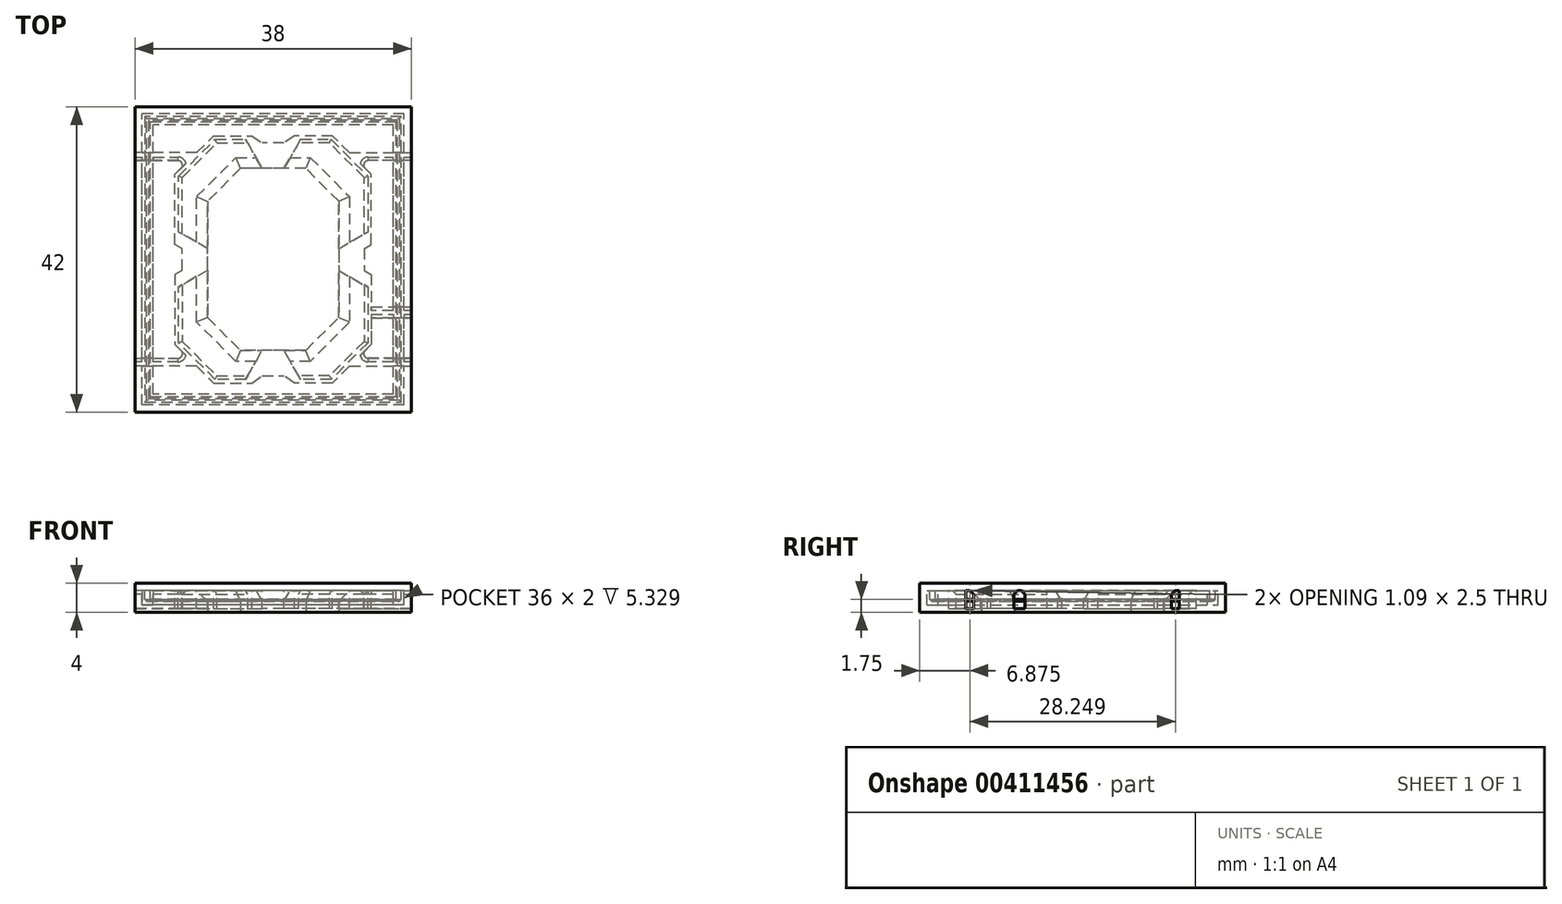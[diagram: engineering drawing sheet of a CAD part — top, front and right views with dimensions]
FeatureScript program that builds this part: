
annotation { "Feature Type Name" : "Feature", "Feature Type Description" : "" }
export const myFeature = defineFeature(function(context is Context, id is Id, definition is map)
    precondition{}
    {
        {
            var Q0;
            Q0=qCreatedBy(makeId("Top.planeOp"),FACE);
            var sketch = newSketch(context, id + "F0", { "sketchPlane" : qUnion([Q0])});
            skLineSegment(sketch, "E0.bottom", {"start": v(19, -21) * mm, "end": v(-19, -21) * mm});
            skLineSegment(sketch, "E0.top", {"start": v(19, 21) * mm, "end": v(-19, 21) * mm});
            skLineSegment(sketch, "E0.left", {"start": v(19, -21) * mm, "end": v(19, 21) * mm});
            skLineSegment(sketch, "E0.right", {"start": v(-19, -21) * mm, "end": v(-19, 21) * mm});
            skPoint(sketch, "E0.middle", {"position": v(0, 0) * mm});
            skLineSegment(sketch, "E1", {"start": v(4.5, 12.5) * mm, "end": v(9, 8) * mm});
            skLineSegment(sketch, "E2", {"start": v(4.5, 12.5) * mm, "end": v(0, 12.5) * mm});
            skLineSegment(sketch, "E3", {"start": v(9, 8) * mm, "end": v(9, 0) * mm});
            skLineSegment(sketch, "E4.MirrorCS", {"start": v(-9, 8) * mm, "end": v(-9, 0) * mm});
            skLineSegment(sketch, "E5.MirrorCS", {"start": v(-4.5, 12.5) * mm, "end": v(-9, 8) * mm});
            skLineSegment(sketch, "E6.MirrorCS", {"start": v(-4.5, 12.5) * mm, "end": v(0, 12.5) * mm});
            skLineSegment(sketch, "E7.MirrorCS", {"start": v(-9, -8) * mm, "end": v(-9, 0) * mm});
            skLineSegment(sketch, "E8.MirrorCS", {"start": v(4.5, -12.5) * mm, "end": v(9, -8) * mm});
            skLineSegment(sketch, "E9.MirrorCS", {"start": v(9, -8) * mm, "end": v(9, 0) * mm});
            skLineSegment(sketch, "E10.MirrorCS", {"start": v(-4.5, -12.5) * mm, "end": v(-9, -8) * mm});
            skLineSegment(sketch, "E11.MirrorCS", {"start": v(-4.5, -12.5) * mm, "end": v(0, -12.5) * mm});
            skLineSegment(sketch, "E12.MirrorCS", {"start": v(4.5, -12.5) * mm, "end": v(0, -12.5) * mm});
            skSolve(sketch);
        }
        {
            var Q0;
            Q0 = qSketchRegion(id + "F0", true);
            extrude(context, id + "F1", {"entities" : qUnion([Q0]), "depth" : 3 * mm, "offsetDistance" : 25 * mm});
        }
        {
            var Q0;
            Q0=makeQuery(id+"F1.opExtrude","CAP_FACE",FACE,{"disambiguationData":[OSD([sQuery(id+"F0.wireOp",EDGE,"E0.bottom"),sQuery(id+"F0.wireOp",EDGE,"E0.top"),sQuery(id+"F0.wireOp",EDGE,"E0.left"),sQuery(id+"F0.wireOp",EDGE,"E0.right"),sQuery(id+"F0.wireOp",EDGE,"E1"),sQuery(id+"F0.wireOp",EDGE,"E2"),sQuery(id+"F0.wireOp",EDGE,"E3"),sQuery(id+"F0.wireOp",EDGE,"E4.MirrorCS"),sQuery(id+"F0.wireOp",EDGE,"E5.MirrorCS"),sQuery(id+"F0.wireOp",EDGE,"E6.MirrorCS"),sQuery(id+"F0.wireOp",EDGE,"E7.MirrorCS"),sQuery(id+"F0.wireOp",EDGE,"E8.MirrorCS"),sQuery(id+"F0.wireOp",EDGE,"E9.MirrorCS"),sQuery(id+"F0.wireOp",EDGE,"E10.MirrorCS"),sQuery(id+"F0.wireOp",EDGE,"E11.MirrorCS"),sQuery(id+"F0.wireOp",EDGE,"E12.MirrorCS")])],"isStart":false});
            var sketch = newSketch(context, id + "F2", { "sketchPlane" : qUnion([Q0])});
            skLineSegment(sketch, "E13", {"start": v(9, 1.5) * mm, "end": v(12.5, 3.5) * mm});
            skLineSegment(sketch, "E14", {"start": v(12.5, 3.5) * mm, "end": v(12.5, 11.26) * mm});
            skLineSegment(sketch, "E15", {"start": v(7.76, 16) * mm, "end": v(3.5, 16) * mm});
            skLineSegment(sketch, "E16", {"start": v(3.5, 16) * mm, "end": v(1.5, 12.5) * mm});
            skLineSegment(sketch, "E17", {"start": v(12.5, 1.5) * mm, "end": v(13.5, 2.07) * mm});
            skLineSegment(sketch, "E18", {"start": v(13.5, 2.07) * mm, "end": v(13.5, 11.67) * mm});
            skLineSegment(sketch, "E19", {"start": v(8.17, 17) * mm, "end": v(2.91, 17) * mm});
            skLineSegment(sketch, "E20", {"start": v(2.91, 17) * mm, "end": v(1.5, 16) * mm});
            skLineSegment(sketch, "E21", {"start": v(1.5, 16) * mm, "end": v(0, 16) * mm});
            skLineSegment(sketch, "E22", {"start": v(1.5, 12.5) * mm, "end": v(0, 12.5) * mm});
            skLineSegment(sketch, "E23", {"start": v(9, 0) * mm, "end": v(9, 1.5) * mm});
            skLineSegment(sketch, "E24", {"start": v(12.5, 0) * mm, "end": v(12.5, 1.5) * mm});
            skLineSegment(sketch, "E25", {"start": v(12.5, 11.26) * mm, "end": v(7.76, 16) * mm});
            skLineSegment(sketch, "E26", {"start": v(13.5, 11.67) * mm, "end": v(12.54, 12.64) * mm});
            skLineSegment(sketch, "E27", {"start": v(10.5, 14.67) * mm, "end": v(19, 14.67) * mm});
            skLineSegment(sketch, "E28", {"start": v(19, 14.67) * mm, "end": v(19, 13.58) * mm});
            skLineSegment(sketch, "E29", {"start": v(19, 13.58) * mm, "end": v(13.06, 13.58) * mm});
            skArc(sketch, "E30", {"start": v(13.06, 13.58) * mm, "mid": v(12.53, 13.25) * mm, "end": v(12.54, 12.64) * mm});
            skLineSegment(sketch, "E31.trimOffspring", {"start": v(10.5, 14.67) * mm, "end": v(8.17, 17) * mm});
            skArc(sketch, "E32.MirrorCS", {"start": v(-13.06, 13.58) * mm, "mid": v(-12.53, 13.25) * mm, "end": v(-12.54, 12.64) * mm});
            skLineSegment(sketch, "E33.MirrorCS", {"start": v(-9, 1.5) * mm, "end": v(-12.5, 3.5) * mm});
            skLineSegment(sketch, "E34.MirrorCS", {"start": v(-7.76, 16) * mm, "end": v(-3.5, 16) * mm});
            skLineSegment(sketch, "E35.MirrorCS", {"start": v(-19, 14.67) * mm, "end": v(-19, 13.58) * mm});
            skLineSegment(sketch, "E36.MirrorCS", {"start": v(-12.5, 3.5) * mm, "end": v(-12.5, 11.26) * mm});
            skLineSegment(sketch, "E37.MirrorCS", {"start": v(-19, 13.58) * mm, "end": v(-13.06, 13.58) * mm});
            skLineSegment(sketch, "E38.MirrorCS", {"start": v(-9, 0) * mm, "end": v(-9, 1.5) * mm});
            skLineSegment(sketch, "E39.MirrorCS", {"start": v(-8.17, 17) * mm, "end": v(-2.91, 17) * mm});
            skLineSegment(sketch, "E40.MirrorCS", {"start": v(-10.5, 14.67) * mm, "end": v(-8.17, 17) * mm});
            skLineSegment(sketch, "E41.MirrorCS", {"start": v(-1.5, 16) * mm, "end": v(0, 16) * mm});
            skLineSegment(sketch, "E42.MirrorCS", {"start": v(-12.5, 11.26) * mm, "end": v(-7.76, 16) * mm});
            skLineSegment(sketch, "E43.MirrorCS", {"start": v(-1.5, 12.5) * mm, "end": v(0, 12.5) * mm});
            skLineSegment(sketch, "E44.MirrorCS", {"start": v(-2.91, 17) * mm, "end": v(-1.5, 16) * mm});
            skLineSegment(sketch, "E45.MirrorCS", {"start": v(-10.5, 14.67) * mm, "end": v(-19, 14.67) * mm});
            skLineSegment(sketch, "E46.MirrorCS", {"start": v(-12.5, 1.5) * mm, "end": v(-13.5, 2.07) * mm});
            skLineSegment(sketch, "E47.MirrorCS", {"start": v(-13.5, 2.07) * mm, "end": v(-13.5, 11.67) * mm});
            skLineSegment(sketch, "E48.MirrorCS", {"start": v(-12.5, 0) * mm, "end": v(-12.5, 1.5) * mm});
            skLineSegment(sketch, "E49.MirrorCS", {"start": v(-3.5, 16) * mm, "end": v(-1.5, 12.5) * mm});
            skLineSegment(sketch, "E50.MirrorCS", {"start": v(-13.5, 11.67) * mm, "end": v(-12.54, 12.64) * mm});
            skLineSegment(sketch, "E51.MirrorCS", {"start": v(-12.5, -1.5) * mm, "end": v(-13.5, -2.07) * mm});
            skLineSegment(sketch, "E52.MirrorCS", {"start": v(19, -14.67) * mm, "end": v(19, -13.58) * mm});
            skLineSegment(sketch, "E53.MirrorCS", {"start": v(-19, -14.67) * mm, "end": v(-19, -13.58) * mm});
            skLineSegment(sketch, "E54.MirrorCS", {"start": v(12.5, -1.5) * mm, "end": v(13.5, -2.07) * mm});
            skArc(sketch, "E55.MirrorCS", {"start": v(-13.06, -13.58) * mm, "mid": v(-12.53, -13.25) * mm, "end": v(-12.54, -12.64) * mm});
            skArc(sketch, "E56.MirrorCS", {"start": v(13.06, -13.58) * mm, "mid": v(12.53, -13.25) * mm, "end": v(12.54, -12.64) * mm});
            skLineSegment(sketch, "E57.MirrorCS", {"start": v(-1.5, -12.5) * mm, "end": v(0, -12.5) * mm});
            skLineSegment(sketch, "E58.MirrorCS", {"start": v(-1.5, -16) * mm, "end": v(0, -16) * mm});
            skLineSegment(sketch, "E59.MirrorCS", {"start": v(-12.5, 0) * mm, "end": v(-12.5, -1.5) * mm});
            skLineSegment(sketch, "E60.MirrorCS", {"start": v(-9, 0) * mm, "end": v(-9, -1.5) * mm});
            skLineSegment(sketch, "E61.MirrorCS", {"start": v(12.5, 0) * mm, "end": v(12.5, -1.5) * mm});
            skLineSegment(sketch, "E62.MirrorCS", {"start": v(9, 0) * mm, "end": v(9, -1.5) * mm});
            skLineSegment(sketch, "E63.MirrorCS", {"start": v(-7.76, -16) * mm, "end": v(-3.5, -16) * mm});
            skLineSegment(sketch, "E64.MirrorCS", {"start": v(3.5, -16) * mm, "end": v(1.5, -12.5) * mm});
            skLineSegment(sketch, "E65.MirrorCS", {"start": v(1.5, -12.5) * mm, "end": v(0, -12.5) * mm});
            skLineSegment(sketch, "E66.MirrorCS", {"start": v(10.5, -14.67) * mm, "end": v(8.17, -17) * mm});
            skLineSegment(sketch, "E67.MirrorCS", {"start": v(7.76, -16) * mm, "end": v(3.5, -16) * mm});
            skLineSegment(sketch, "E68.MirrorCS", {"start": v(13.5, -11.67) * mm, "end": v(12.54, -12.64) * mm});
            skLineSegment(sketch, "E69.MirrorCS", {"start": v(12.5, -11.26) * mm, "end": v(7.76, -16) * mm});
            skLineSegment(sketch, "E70.MirrorCS", {"start": v(-2.91, -17) * mm, "end": v(-1.5, -16) * mm});
            skLineSegment(sketch, "E71.MirrorCS", {"start": v(19, -13.58) * mm, "end": v(13.06, -13.58) * mm});
            skLineSegment(sketch, "E72.MirrorCS", {"start": v(-13.5, -2.07) * mm, "end": v(-13.5, -11.67) * mm});
            skLineSegment(sketch, "E73.MirrorCS", {"start": v(-12.5, -3.5) * mm, "end": v(-12.5, -11.26) * mm});
            skLineSegment(sketch, "E74.MirrorCS", {"start": v(2.91, -17) * mm, "end": v(1.5, -16) * mm});
            skLineSegment(sketch, "E75.MirrorCS", {"start": v(13.5, -2.07) * mm, "end": v(13.5, -11.67) * mm});
            skLineSegment(sketch, "E76.MirrorCS", {"start": v(-8.17, -17) * mm, "end": v(-2.91, -17) * mm});
            skLineSegment(sketch, "E77.MirrorCS", {"start": v(-9, -1.5) * mm, "end": v(-12.5, -3.5) * mm});
            skLineSegment(sketch, "E78.MirrorCS", {"start": v(1.5, -16) * mm, "end": v(0, -16) * mm});
            skLineSegment(sketch, "E79.MirrorCS", {"start": v(-3.5, -16) * mm, "end": v(-1.5, -12.5) * mm});
            skLineSegment(sketch, "E80.MirrorCS", {"start": v(-12.5, -11.26) * mm, "end": v(-7.76, -16) * mm});
            skLineSegment(sketch, "E81.MirrorCS", {"start": v(8.17, -17) * mm, "end": v(2.91, -17) * mm});
            skLineSegment(sketch, "E82.MirrorCS", {"start": v(-19, -13.58) * mm, "end": v(-13.06, -13.58) * mm});
            skLineSegment(sketch, "E83.MirrorCS", {"start": v(10.5, -14.67) * mm, "end": v(19, -14.67) * mm});
            skLineSegment(sketch, "E84.MirrorCS", {"start": v(-10.5, -14.67) * mm, "end": v(-8.17, -17) * mm});
            skLineSegment(sketch, "E85.MirrorCS", {"start": v(12.5, -3.5) * mm, "end": v(12.5, -11.26) * mm});
            skLineSegment(sketch, "E86.MirrorCS", {"start": v(9, -1.5) * mm, "end": v(12.5, -3.5) * mm});
            skLineSegment(sketch, "E87.MirrorCS", {"start": v(-13.5, -11.67) * mm, "end": v(-12.54, -12.64) * mm});
            skLineSegment(sketch, "E88.MirrorCS", {"start": v(-10.5, -14.67) * mm, "end": v(-19, -14.67) * mm});
            skLineSegment(sketch, "E89.bottom", {"start": v(13.5, -6.55) * mm, "end": v(19, -6.55) * mm});
            skLineSegment(sketch, "E89.top", {"start": v(13.5, -8.05) * mm, "end": v(19, -8.05) * mm});
            skLineSegment(sketch, "E89.left", {"start": v(13.5, -6.55) * mm, "end": v(13.5, -8.05) * mm});
            skLineSegment(sketch, "E89.right", {"start": v(19, -6.55) * mm, "end": v(19, -8.05) * mm});
            skSolve(sketch);
        }
        {
            var Q0;
            Q0 = qSketchRegion(id + "F2", true);
            extrude(context, id + "F3", {"entities" : qUnion([Q0]), "oppositeDirection" : true, "depth" : 2.5 * mm, "offsetDistance" : 25 * mm});
        }
        {
            var Q0;
            Q0=makeQuery(id+"F1.opExtrude","CAP_EDGE",EDGE,{"disambiguationData":[OSD([sQuery(id+"F0.wireOp",EDGE,"E5.MirrorCS")])],"isStart":false});
            var Q1;
            {var subQ0=sQuery(id+"F0.wireOp",EDGE,"E6.MirrorCS");var subQ1=sQuery(id+"F0.wireOp",EDGE,"E5.MirrorCS");var subQ2=sQuery(id+"F0.wireOp",EDGE,"E2");Q1=makeQuery(id+"F3.boolean.opBoolean","SPLIT",EDGE,{"disambiguationData":[TD([makeQuery(id+"F1.opExtrude","SWEPT_FACE",FACE,{"disambiguationData":[OSD([subQ1])]})])],"derivedFrom":makeQuery(id+"F1.opExtrude","CAP_EDGE",EDGE,{"disambiguationData":[OSD([subQ2,subQ0])],"isStart":false})});}
            var Q2;
            {var subQ0=sQuery(id+"F0.wireOp",EDGE,"E7.MirrorCS");var subQ1=sQuery(id+"F0.wireOp",EDGE,"E5.MirrorCS");var subQ2=sQuery(id+"F0.wireOp",EDGE,"E4.MirrorCS");Q2=makeQuery(id+"F3.boolean.opBoolean","SPLIT",EDGE,{"disambiguationData":[TD([makeQuery(id+"F1.opExtrude","SWEPT_FACE",FACE,{"disambiguationData":[OSD([subQ1])]})])],"derivedFrom":makeQuery(id+"F1.opExtrude","CAP_EDGE",EDGE,{"disambiguationData":[OSD([subQ2,subQ0])],"isStart":false})});}
            var Q3;
            {var subQ0=sQuery(id+"F0.wireOp",EDGE,"E6.MirrorCS");var subQ1=sQuery(id+"F0.wireOp",EDGE,"E2");var subQ2=sQuery(id+"F0.wireOp",EDGE,"E1");Q3=makeQuery(id+"F3.boolean.opBoolean","SPLIT",EDGE,{"disambiguationData":[TD([makeQuery(id+"F1.opExtrude","SWEPT_FACE",FACE,{"disambiguationData":[OSD([subQ2])]})])],"derivedFrom":makeQuery(id+"F1.opExtrude","CAP_EDGE",EDGE,{"disambiguationData":[OSD([subQ1,subQ0])],"isStart":false})});}
            var Q4;
            Q4=makeQuery(id+"F1.opExtrude","CAP_EDGE",EDGE,{"disambiguationData":[OSD([sQuery(id+"F0.wireOp",EDGE,"E1")])],"isStart":false});
            var Q5;
            {var subQ0=sQuery(id+"F0.wireOp",EDGE,"E9.MirrorCS");var subQ1=sQuery(id+"F0.wireOp",EDGE,"E3");var subQ2=sQuery(id+"F0.wireOp",EDGE,"E1");Q5=makeQuery(id+"F3.boolean.opBoolean","SPLIT",EDGE,{"disambiguationData":[TD([makeQuery(id+"F1.opExtrude","SWEPT_FACE",FACE,{"disambiguationData":[OSD([subQ2])]})])],"derivedFrom":makeQuery(id+"F1.opExtrude","CAP_EDGE",EDGE,{"disambiguationData":[OSD([subQ1,subQ0])],"isStart":false})});}
            var Q6;
            {var subQ0=sQuery(id+"F0.wireOp",EDGE,"E9.MirrorCS");var subQ1=sQuery(id+"F0.wireOp",EDGE,"E8.MirrorCS");var subQ2=sQuery(id+"F0.wireOp",EDGE,"E3");Q6=makeQuery(id+"F3.boolean.opBoolean","SPLIT",EDGE,{"disambiguationData":[TD([makeQuery(id+"F1.opExtrude","SWEPT_FACE",FACE,{"disambiguationData":[OSD([subQ1])]})])],"derivedFrom":makeQuery(id+"F1.opExtrude","CAP_EDGE",EDGE,{"disambiguationData":[OSD([subQ2,subQ0])],"isStart":false})});}
            var Q7;
            Q7=makeQuery(id+"F1.opExtrude","CAP_EDGE",EDGE,{"disambiguationData":[OSD([sQuery(id+"F0.wireOp",EDGE,"E8.MirrorCS")])],"isStart":false});
            var Q8;
            {var subQ0=sQuery(id+"F0.wireOp",EDGE,"E12.MirrorCS");var subQ1=sQuery(id+"F0.wireOp",EDGE,"E11.MirrorCS");var subQ2=sQuery(id+"F0.wireOp",EDGE,"E8.MirrorCS");Q8=makeQuery(id+"F3.boolean.opBoolean","SPLIT",EDGE,{"disambiguationData":[TD([makeQuery(id+"F1.opExtrude","SWEPT_FACE",FACE,{"disambiguationData":[OSD([subQ2])]})])],"derivedFrom":makeQuery(id+"F1.opExtrude","CAP_EDGE",EDGE,{"disambiguationData":[OSD([subQ1,subQ0])],"isStart":false})});}
            var Q9;
            {var subQ0=sQuery(id+"F0.wireOp",EDGE,"E12.MirrorCS");var subQ1=sQuery(id+"F0.wireOp",EDGE,"E11.MirrorCS");var subQ2=sQuery(id+"F0.wireOp",EDGE,"E10.MirrorCS");Q9=makeQuery(id+"F3.boolean.opBoolean","SPLIT",EDGE,{"disambiguationData":[TD([makeQuery(id+"F1.opExtrude","SWEPT_FACE",FACE,{"disambiguationData":[OSD([subQ2])]})])],"derivedFrom":makeQuery(id+"F1.opExtrude","CAP_EDGE",EDGE,{"disambiguationData":[OSD([subQ1,subQ0])],"isStart":false})});}
            var Q10;
            Q10=makeQuery(id+"F1.opExtrude","CAP_EDGE",EDGE,{"disambiguationData":[OSD([sQuery(id+"F0.wireOp",EDGE,"E10.MirrorCS")])],"isStart":false});
            var Q11;
            {var subQ0=sQuery(id+"F0.wireOp",EDGE,"E10.MirrorCS");var subQ1=sQuery(id+"F0.wireOp",EDGE,"E7.MirrorCS");var subQ2=sQuery(id+"F0.wireOp",EDGE,"E4.MirrorCS");Q11=makeQuery(id+"F3.boolean.opBoolean","SPLIT",EDGE,{"disambiguationData":[TD([makeQuery(id+"F1.opExtrude","SWEPT_FACE",FACE,{"disambiguationData":[OSD([subQ0])]})])],"derivedFrom":makeQuery(id+"F1.opExtrude","CAP_EDGE",EDGE,{"disambiguationData":[OSD([subQ2,subQ1])],"isStart":false})});}
            chamfer(context, id + "F4", {"entities" : qUnion([Q0, Q1, Q2, Q3, Q4, Q5, Q6, Q7, Q8, Q9, Q10, Q11]), "width" : 1.5 * mm, "tangentPropagation" : true});
        }
        {
            var Q0;
            Q0=makeQuery(id+"F3.opExtrude","CAP_EDGE",EDGE,{"disambiguationData":[OSD([sQuery(id+"F2.wireOp",EDGE,"E14")])],"isStart":true});
            var Q1;
            Q1=makeQuery(id+"F3.opExtrude","CAP_EDGE",EDGE,{"disambiguationData":[OSD([sQuery(id+"F2.wireOp",EDGE,"E25")])],"isStart":true});
            var Q2;
            Q2=makeQuery(id+"F3.opExtrude","CAP_EDGE",EDGE,{"disambiguationData":[OSD([sQuery(id+"F2.wireOp",EDGE,"E15")])],"isStart":true});
            var Q3;
            Q3=makeQuery(id+"F3.opExtrude","CAP_EDGE",EDGE,{"disambiguationData":[OSD([sQuery(id+"F2.wireOp",EDGE,"E34.MirrorCS")])],"isStart":true});
            var Q4;
            Q4=makeQuery(id+"F3.opExtrude","CAP_EDGE",EDGE,{"disambiguationData":[OSD([sQuery(id+"F2.wireOp",EDGE,"E42.MirrorCS")])],"isStart":true});
            var Q5;
            Q5=makeQuery(id+"F3.opExtrude","CAP_EDGE",EDGE,{"disambiguationData":[OSD([sQuery(id+"F2.wireOp",EDGE,"E36.MirrorCS")])],"isStart":true});
            var Q6;
            Q6=makeQuery(id+"F3.opExtrude","CAP_EDGE",EDGE,{"disambiguationData":[OSD([sQuery(id+"F2.wireOp",EDGE,"E73.MirrorCS")])],"isStart":true});
            var Q7;
            Q7=makeQuery(id+"F3.opExtrude","CAP_EDGE",EDGE,{"disambiguationData":[OSD([sQuery(id+"F2.wireOp",EDGE,"E80.MirrorCS")])],"isStart":true});
            var Q8;
            Q8=makeQuery(id+"F3.opExtrude","CAP_EDGE",EDGE,{"disambiguationData":[OSD([sQuery(id+"F2.wireOp",EDGE,"E63.MirrorCS")])],"isStart":true});
            var Q9;
            Q9=makeQuery(id+"F3.opExtrude","CAP_EDGE",EDGE,{"disambiguationData":[OSD([sQuery(id+"F2.wireOp",EDGE,"E67.MirrorCS")])],"isStart":true});
            var Q10;
            Q10=makeQuery(id+"F3.opExtrude","CAP_EDGE",EDGE,{"disambiguationData":[OSD([sQuery(id+"F2.wireOp",EDGE,"E69.MirrorCS")])],"isStart":true});
            var Q11;
            Q11=makeQuery(id+"F3.opExtrude","CAP_EDGE",EDGE,{"disambiguationData":[OSD([sQuery(id+"F2.wireOp",EDGE,"E85.MirrorCS")])],"isStart":true});
            var Q12;
            Q12=makeQuery(id+"F3.opExtrude","CAP_EDGE",EDGE,{"disambiguationData":[OSD([sQuery(id+"F2.wireOp",EDGE,"E37.MirrorCS")])],"isStart":true});
            var Q13;
            Q13=makeQuery(id+"F3.opExtrude","CAP_EDGE",EDGE,{"disambiguationData":[OSD([sQuery(id+"F2.wireOp",EDGE,"E82.MirrorCS")])],"isStart":true});
            var Q14;
            Q14=makeQuery(id+"F3.opExtrude","CAP_EDGE",EDGE,{"disambiguationData":[OSD([sQuery(id+"F2.wireOp",EDGE,"E71.MirrorCS")])],"isStart":true});
            var Q15;
            Q15=makeQuery(id+"F3.opExtrude","CAP_EDGE",EDGE,{"disambiguationData":[OSD([sQuery(id+"F2.wireOp",EDGE,"E29")])],"isStart":true});
            var Q16;
            Q16=makeQuery(id+"F3.opExtrude","CAP_EDGE",EDGE,{"disambiguationData":[OSD([sQuery(id+"F2.wireOp",EDGE,"E89.top")])],"isStart":true});
            var Q17;
            Q17=makeQuery(id+"F3.opExtrude","CAP_EDGE",EDGE,{"disambiguationData":[OSD([sQuery(id+"F2.wireOp",EDGE,"E89.bottom")])],"isStart":true});
            chamfer(context, id + "F5", {"entities" : qUnion([Q0, Q1, Q2, Q3, Q4, Q5, Q6, Q7, Q8, Q9, Q10, Q11, Q12, Q13, Q14, Q15, Q16, Q17]), "width" : .5 * mm, "tangentPropagation" : true});
        }
        {
            var Q0;
            Q0=makeQuery(id+"F3.opExtrude","SWEPT_BODY",BODY,{"disambiguationData":[OSD([sQuery(id+"F2.wireOp",EDGE,"E13"),sQuery(id+"F2.wireOp",EDGE,"E14"),sQuery(id+"F2.wireOp",EDGE,"E15"),sQuery(id+"F2.wireOp",EDGE,"E16"),sQuery(id+"F2.wireOp",EDGE,"E17"),sQuery(id+"F2.wireOp",EDGE,"E18"),sQuery(id+"F2.wireOp",EDGE,"E19"),sQuery(id+"F2.wireOp",EDGE,"E20"),sQuery(id+"F2.wireOp",EDGE,"E21"),sQuery(id+"F2.wireOp",EDGE,"E22"),sQuery(id+"F2.wireOp",EDGE,"E23"),sQuery(id+"F2.wireOp",EDGE,"E24"),sQuery(id+"F2.wireOp",EDGE,"E25"),sQuery(id+"F2.wireOp",EDGE,"E26"),sQuery(id+"F2.wireOp",EDGE,"E27"),sQuery(id+"F2.wireOp",EDGE,"E28"),sQuery(id+"F2.wireOp",EDGE,"E29"),sQuery(id+"F2.wireOp",EDGE,"E30"),sQuery(id+"F2.wireOp",EDGE,"E31.trimOffspring"),sQuery(id+"F2.wireOp",EDGE,"E32.MirrorCS"),sQuery(id+"F2.wireOp",EDGE,"E33.MirrorCS"),sQuery(id+"F2.wireOp",EDGE,"E34.MirrorCS"),sQuery(id+"F2.wireOp",EDGE,"E35.MirrorCS"),sQuery(id+"F2.wireOp",EDGE,"E36.MirrorCS"),sQuery(id+"F2.wireOp",EDGE,"E37.MirrorCS"),sQuery(id+"F2.wireOp",EDGE,"E38.MirrorCS"),sQuery(id+"F2.wireOp",EDGE,"E39.MirrorCS"),sQuery(id+"F2.wireOp",EDGE,"E40.MirrorCS"),sQuery(id+"F2.wireOp",EDGE,"E41.MirrorCS"),sQuery(id+"F2.wireOp",EDGE,"E42.MirrorCS"),sQuery(id+"F2.wireOp",EDGE,"E43.MirrorCS"),sQuery(id+"F2.wireOp",EDGE,"E44.MirrorCS"),sQuery(id+"F2.wireOp",EDGE,"E45.MirrorCS"),sQuery(id+"F2.wireOp",EDGE,"E46.MirrorCS"),sQuery(id+"F2.wireOp",EDGE,"E47.MirrorCS"),sQuery(id+"F2.wireOp",EDGE,"E48.MirrorCS"),sQuery(id+"F2.wireOp",EDGE,"E49.MirrorCS"),sQuery(id+"F2.wireOp",EDGE,"E50.MirrorCS"),sQuery(id+"F2.wireOp",EDGE,"E51.MirrorCS"),sQuery(id+"F2.wireOp",EDGE,"E52.MirrorCS"),sQuery(id+"F2.wireOp",EDGE,"E53.MirrorCS"),sQuery(id+"F2.wireOp",EDGE,"E54.MirrorCS"),sQuery(id+"F2.wireOp",EDGE,"E55.MirrorCS"),sQuery(id+"F2.wireOp",EDGE,"E56.MirrorCS"),sQuery(id+"F2.wireOp",EDGE,"E57.MirrorCS"),sQuery(id+"F2.wireOp",EDGE,"E58.MirrorCS"),sQuery(id+"F2.wireOp",EDGE,"E59.MirrorCS"),sQuery(id+"F2.wireOp",EDGE,"E60.MirrorCS"),sQuery(id+"F2.wireOp",EDGE,"E61.MirrorCS"),sQuery(id+"F2.wireOp",EDGE,"E62.MirrorCS"),sQuery(id+"F2.wireOp",EDGE,"E63.MirrorCS"),sQuery(id+"F2.wireOp",EDGE,"E64.MirrorCS"),sQuery(id+"F2.wireOp",EDGE,"E65.MirrorCS"),sQuery(id+"F2.wireOp",EDGE,"E66.MirrorCS"),sQuery(id+"F2.wireOp",EDGE,"E67.MirrorCS"),sQuery(id+"F2.wireOp",EDGE,"E68.MirrorCS"),sQuery(id+"F2.wireOp",EDGE,"E69.MirrorCS"),sQuery(id+"F2.wireOp",EDGE,"E70.MirrorCS"),sQuery(id+"F2.wireOp",EDGE,"E71.MirrorCS"),sQuery(id+"F2.wireOp",EDGE,"E72.MirrorCS"),sQuery(id+"F2.wireOp",EDGE,"E73.MirrorCS"),sQuery(id+"F2.wireOp",EDGE,"E74.MirrorCS"),sQuery(id+"F2.wireOp",EDGE,"E75.MirrorCS"),sQuery(id+"F2.wireOp",EDGE,"E76.MirrorCS"),sQuery(id+"F2.wireOp",EDGE,"E77.MirrorCS"),sQuery(id+"F2.wireOp",EDGE,"E78.MirrorCS"),sQuery(id+"F2.wireOp",EDGE,"E79.MirrorCS"),sQuery(id+"F2.wireOp",EDGE,"E80.MirrorCS"),sQuery(id+"F2.wireOp",EDGE,"E81.MirrorCS"),sQuery(id+"F2.wireOp",EDGE,"E82.MirrorCS"),sQuery(id+"F2.wireOp",EDGE,"E83.MirrorCS"),sQuery(id+"F2.wireOp",EDGE,"E84.MirrorCS"),sQuery(id+"F2.wireOp",EDGE,"E85.MirrorCS"),sQuery(id+"F2.wireOp",EDGE,"E86.MirrorCS"),sQuery(id+"F2.wireOp",EDGE,"E87.MirrorCS"),sQuery(id+"F2.wireOp",EDGE,"E88.MirrorCS")])]});
            var Q1;
            Q1=makeQuery(id+"F1.opExtrude","SWEPT_BODY",BODY,{"disambiguationData":[OSD([sQuery(id+"F0.wireOp",EDGE,"E0.bottom"),sQuery(id+"F0.wireOp",EDGE,"E0.top"),sQuery(id+"F0.wireOp",EDGE,"E0.left"),sQuery(id+"F0.wireOp",EDGE,"E0.right"),sQuery(id+"F0.wireOp",EDGE,"E1"),sQuery(id+"F0.wireOp",EDGE,"E2"),sQuery(id+"F0.wireOp",EDGE,"E3"),sQuery(id+"F0.wireOp",EDGE,"E4.MirrorCS"),sQuery(id+"F0.wireOp",EDGE,"E5.MirrorCS"),sQuery(id+"F0.wireOp",EDGE,"E6.MirrorCS"),sQuery(id+"F0.wireOp",EDGE,"E7.MirrorCS"),sQuery(id+"F0.wireOp",EDGE,"E8.MirrorCS"),sQuery(id+"F0.wireOp",EDGE,"E9.MirrorCS"),sQuery(id+"F0.wireOp",EDGE,"E10.MirrorCS"),sQuery(id+"F0.wireOp",EDGE,"E11.MirrorCS"),sQuery(id+"F0.wireOp",EDGE,"E12.MirrorCS")])]});
            booleanBodies(context, id + "F6", {"operationType" : BooleanOperationType.SUBTRACTION, "tools" : qUnion([Q0]), "targets" : qUnion([Q1])});
        }
        {
            var Q0;
            {var subQ0=sQuery(id+"F0.wireOp",EDGE,"E0.right");Q0=makeQuery(id+"F6.opBoolean","SPLIT",FACE,{"disambiguationData":[TD([makeQuery(id+"F3.opExtrude","SWEPT_FACE",FACE,{"disambiguationData":[OSD([sQuery(id+"F2.wireOp",EDGE,"E46.MirrorCS")])]})])],"derivedFrom":makeQuery(id+"F1.opExtrude","CAP_FACE",FACE,{"disambiguationData":[OSD([sQuery(id+"F0.wireOp",EDGE,"E0.bottom"),sQuery(id+"F0.wireOp",EDGE,"E0.top"),sQuery(id+"F0.wireOp",EDGE,"E0.left"),subQ0,sQuery(id+"F0.wireOp",EDGE,"E1"),sQuery(id+"F0.wireOp",EDGE,"E2"),sQuery(id+"F0.wireOp",EDGE,"E3"),sQuery(id+"F0.wireOp",EDGE,"E4.MirrorCS"),sQuery(id+"F0.wireOp",EDGE,"E5.MirrorCS"),sQuery(id+"F0.wireOp",EDGE,"E6.MirrorCS"),sQuery(id+"F0.wireOp",EDGE,"E7.MirrorCS"),sQuery(id+"F0.wireOp",EDGE,"E8.MirrorCS"),sQuery(id+"F0.wireOp",EDGE,"E9.MirrorCS"),sQuery(id+"F0.wireOp",EDGE,"E10.MirrorCS"),sQuery(id+"F0.wireOp",EDGE,"E11.MirrorCS"),sQuery(id+"F0.wireOp",EDGE,"E12.MirrorCS")])],"isStart":false})});}
            var sketch = newSketch(context, id + "F7", { "sketchPlane" : qUnion([Q0])});
            skLineSegment(sketch, "E90.bottom", {"start": v(18, -20) * mm, "end": v(-18, -20) * mm});
            skLineSegment(sketch, "E90.top", {"start": v(18, 20) * mm, "end": v(-18, 20) * mm});
            skLineSegment(sketch, "E90.left", {"start": v(18, -20) * mm, "end": v(18, 20) * mm});
            skLineSegment(sketch, "E90.right", {"start": v(-18, -20) * mm, "end": v(-18, 20) * mm});
            skPoint(sketch, "E90.middle", {"position": v(0, 0) * mm});
            skLineSegment(sketch, "E91.bottom", {"start": v(16.5, -18.5) * mm, "end": v(-16.5, -18.5) * mm});
            skLineSegment(sketch, "E91.top", {"start": v(16.5, 18.5) * mm, "end": v(-16.5, 18.5) * mm});
            skLineSegment(sketch, "E91.left", {"start": v(16.5, -18.5) * mm, "end": v(16.5, 18.5) * mm});
            skLineSegment(sketch, "E91.right", {"start": v(-16.5, -18.5) * mm, "end": v(-16.5, 18.5) * mm});
            skSolve(sketch);
        }
        {
            var Q0;
            Q0 = qSketchRegion(id + "F7", true);
            extrude(context, id + "F8", {"entities" : qUnion([Q0]), "operationType" : NewBodyOperationType.REMOVE, "oppositeDirection" : true, "depth" : 2 * mm, "offsetDistance" : 25 * mm});
        }
        {
            var Q0;
            {var subQ0=sQuery(id+"F0.wireOp",EDGE,"E7.MirrorCS");var subQ1=sQuery(id+"F0.wireOp",EDGE,"E4.MirrorCS");var subQ2=sQuery(id+"F0.wireOp",EDGE,"E6.MirrorCS");var subQ3=sQuery(id+"F0.wireOp",EDGE,"E2");var subQ4=sQuery(id+"F0.wireOp",EDGE,"E5.MirrorCS");Q0=makeQuery(id+"F6.opBoolean","SPLIT",FACE,{"disambiguationData":[TD([makeQuery(id+"F3.opExtrude","SWEPT_FACE",FACE,{"disambiguationData":[OSD([sQuery(id+"F2.wireOp",EDGE,"E33.MirrorCS")])]})])],"derivedFrom":makeQuery(id+"F1.opExtrude","CAP_FACE",FACE,{"disambiguationData":[OSD([sQuery(id+"F0.wireOp",EDGE,"E0.bottom"),sQuery(id+"F0.wireOp",EDGE,"E0.top"),sQuery(id+"F0.wireOp",EDGE,"E0.left"),sQuery(id+"F0.wireOp",EDGE,"E0.right"),sQuery(id+"F0.wireOp",EDGE,"E1"),subQ3,sQuery(id+"F0.wireOp",EDGE,"E3"),subQ1,subQ4,subQ2,subQ0,sQuery(id+"F0.wireOp",EDGE,"E8.MirrorCS"),sQuery(id+"F0.wireOp",EDGE,"E9.MirrorCS"),sQuery(id+"F0.wireOp",EDGE,"E10.MirrorCS"),sQuery(id+"F0.wireOp",EDGE,"E11.MirrorCS"),sQuery(id+"F0.wireOp",EDGE,"E12.MirrorCS")])],"isStart":false})});}
            var sketch = newSketch(context, id + "F9", { "sketchPlane" : qUnion([Q0])});
            skLineSegment(sketch, "E92.bottom", {"start": v(17.62, -19.62) * mm, "end": v(-17.62, -19.63) * mm});
            skLineSegment(sketch, "E92.top", {"start": v(17.62, 19.63) * mm, "end": v(-17.62, 19.62) * mm});
            skLineSegment(sketch, "E92.left", {"start": v(17.62, -19.62) * mm, "end": v(17.62, 19.63) * mm});
            skLineSegment(sketch, "E92.right", {"start": v(-17.62, -19.63) * mm, "end": v(-17.62, 19.62) * mm});
            skPoint(sketch, "E92.middle", {"position": v(0, 0) * mm});
            skLineSegment(sketch, "E93.bottom", {"start": v(16.88, -18.88) * mm, "end": v(-16.88, -18.88) * mm});
            skLineSegment(sketch, "E93.top", {"start": v(16.88, 18.88) * mm, "end": v(-16.88, 18.87) * mm});
            skLineSegment(sketch, "E93.left", {"start": v(16.88, -18.87) * mm, "end": v(16.88, 18.88) * mm});
            skLineSegment(sketch, "E93.right", {"start": v(-16.88, -18.88) * mm, "end": v(-16.88, 18.88) * mm});
            skSolve(sketch);
        }
        {
            var Q0;
            Q0 = qSketchRegion(id + "F9", true);
            extrude(context, id + "F10", {"entities" : qUnion([Q0]), "oppositeDirection" : true, "depth" : 1.5 * mm, "offsetDistance" : 25 * mm});
        }
        {
            var Q0;
            Q0=makeQuery(id+"F10.opExtrude","CAP_FACE",FACE,{"disambiguationData":[OSD([sQuery(id+"F9.wireOp",EDGE,"E92.bottom"),sQuery(id+"F9.wireOp",EDGE,"E92.top"),sQuery(id+"F9.wireOp",EDGE,"E92.left"),sQuery(id+"F9.wireOp",EDGE,"E92.right"),sQuery(id+"F9.wireOp",EDGE,"E93.bottom"),sQuery(id+"F9.wireOp",EDGE,"E93.top"),sQuery(id+"F9.wireOp",EDGE,"E93.left"),sQuery(id+"F9.wireOp",EDGE,"E93.right")])],"isStart":false});
            chamfer(context, id + "F11", {"entities" : qUnion([Q0]), "width" : .25 * mm, "tangentPropagation" : true});
        }
        {
            var Q0;
            Q0=makeQuery(id+"F10.opExtrude","CAP_FACE",FACE,{"disambiguationData":[OSD([sQuery(id+"F9.wireOp",EDGE,"E92.bottom"),sQuery(id+"F9.wireOp",EDGE,"E92.top"),sQuery(id+"F9.wireOp",EDGE,"E92.left"),sQuery(id+"F9.wireOp",EDGE,"E92.right"),sQuery(id+"F9.wireOp",EDGE,"E93.bottom"),sQuery(id+"F9.wireOp",EDGE,"E93.top"),sQuery(id+"F9.wireOp",EDGE,"E93.left"),sQuery(id+"F9.wireOp",EDGE,"E93.right")])],"isStart":true});
            var sketch = newSketch(context, id + "F12", { "sketchPlane" : qUnion([Q0])});
            skLineSegment(sketch, "E94.bottom", {"start": v(19, -21) * mm, "end": v(-19, -21) * mm});
            skLineSegment(sketch, "E94.top", {"start": v(19, 21) * mm, "end": v(-19, 21) * mm});
            skLineSegment(sketch, "E94.left", {"start": v(19, -21) * mm, "end": v(19, 21) * mm});
            skLineSegment(sketch, "E94.right", {"start": v(-19, -21) * mm, "end": v(-19, 21) * mm});
            skPoint(sketch, "E94.middle", {"position": v(0, 0) * mm});
            skSolve(sketch);
        }
        {
            var Q0;
            Q0 = qSketchRegion(id + "F12", true);
            extrude(context, id + "F13", {"entities" : qUnion([Q0]), "operationType" : NewBodyOperationType.ADD, "depth" : 1 * mm, "offsetDistance" : 25 * mm});
        }
    });
